SOLIDWORKS PART (.sldprt)
format: sldprt  version: not decoded by parser v0  size: 462,336 bytes
history: native  units: mm
features: sketch x14, extrude x11, plane x3, cut_extrude x3, fillet x3, mirror x2, material x1 (+10 scaffold rows collapsed)
feature tree (47):
  scaffold x10  (default folders/planes/origin — collapsed)
  material  "材质 <未指定>"
  plane  "前视基准面"
  plane  "上视基准面"
  plane  "右视基准面"
  sketch  "草图1"  dims[c1.D1=~4.672692mm c1.D2=~220.041303mm c2.D1=12.0mm c2.D2=4.0mm c2.D3=200.0mm c3.D1=4.0mm]
  extrude  "凸台-拉伸1"  Depth=45.75mm
  sketch  "草图2"  dims[c1.D1=~6.01008mm c1.D2=~32.253161mm c2.D1=30.0mm c2.D2=8.0mm]
  extrude  "凸台-拉伸2"  Depth=4mm
  sketch  "草图3"  dims[D2=10.0mm D1=0.0mm]
  extrude  "凸台-拉伸3"  Depth=4mm
  sketch  "草图4"  dims[D1=0.0mm]
  extrude  "凸台-拉伸4"  Depth=4mm
  sketch  "草图5"  dims[D1=~27.521233mm]
  cut_extrude  "切除-拉伸1"  Depth=64.8mm
  mirror  "镜向1"
  sketch  "草图6"  dims[c1.D1=~21.890558mm c1.D2=~53.646932mm c2.D1=50.0mm c2.D2=25.0mm c2.D3=10.0mm c2.D4=4.0mm c3.D3=10.0mm c3.D4=4.0mm c4.D3=10.0mm c4.D4=4.0mm c5.D3=~0.262453mm]
  extrude  "凸台-拉伸5"  Depth=4mm
  sketch  "草图7"  dims[D1=20.0mm]
  extrude  "凸台-拉伸6"  Depth=4mm
  sketch  "草图8"  dims[D1=0.0mm]
  extrude  "凸台-拉伸7"  Depth=4mm
  mirror  "镜向2"
  fillet  "圆角1"  Radius=25mm
  sketch  "草图12"  dims[c1.D1=~6.91462mm c1.D3=4.0mm c2.D1=15.0mm c2.D2=15.0mm c3.D1=15.0mm c3.D4=~19.951306mm c4.D1=4.0 c4.D2=3.0]
  cut_extrude  "切除-拉伸5"  Depth=13mm
  sketch  "草图14"  dims[c1.D1=~34.063678mm c1.D2=21.0mm c2.D1=43.0mm c2.D2=20.85mm c3.D1=3.0mm]
  extrude  "凸台-拉伸8"  Depth=10mm
  sketch  "草图15"  dims[D1=0.0mm]
  extrude  "凸台-拉伸9"  Depth=2.35mm
  sketch  "草图18"  dims[c1.D1=~38.529678mm c1.D2=~8.686659mm c2.D1=9.0mm c2.D2=9.0mm]
  extrude  "凸台-拉伸10"  Depth=3mm
  sketch  "草图19"  dims[D1=0.0mm D2=0.0mm]
  extrude  "凸台-拉伸11"  Depth=3mm
  sketch  "草图20"  dims[D1=~18.552427mm]
  cut_extrude  "切除-拉伸6"  Depth=38mm
  fillet  "圆角2"  Radius=5mm
  fillet  "圆角3"  Radius=3mm
decode coverage: 31 of 33 modeling features carry decoded parameters
note: ~ marks probable driven/reference dimensions
note: suppression state not decoded; provenance and decode notes live in map.json
